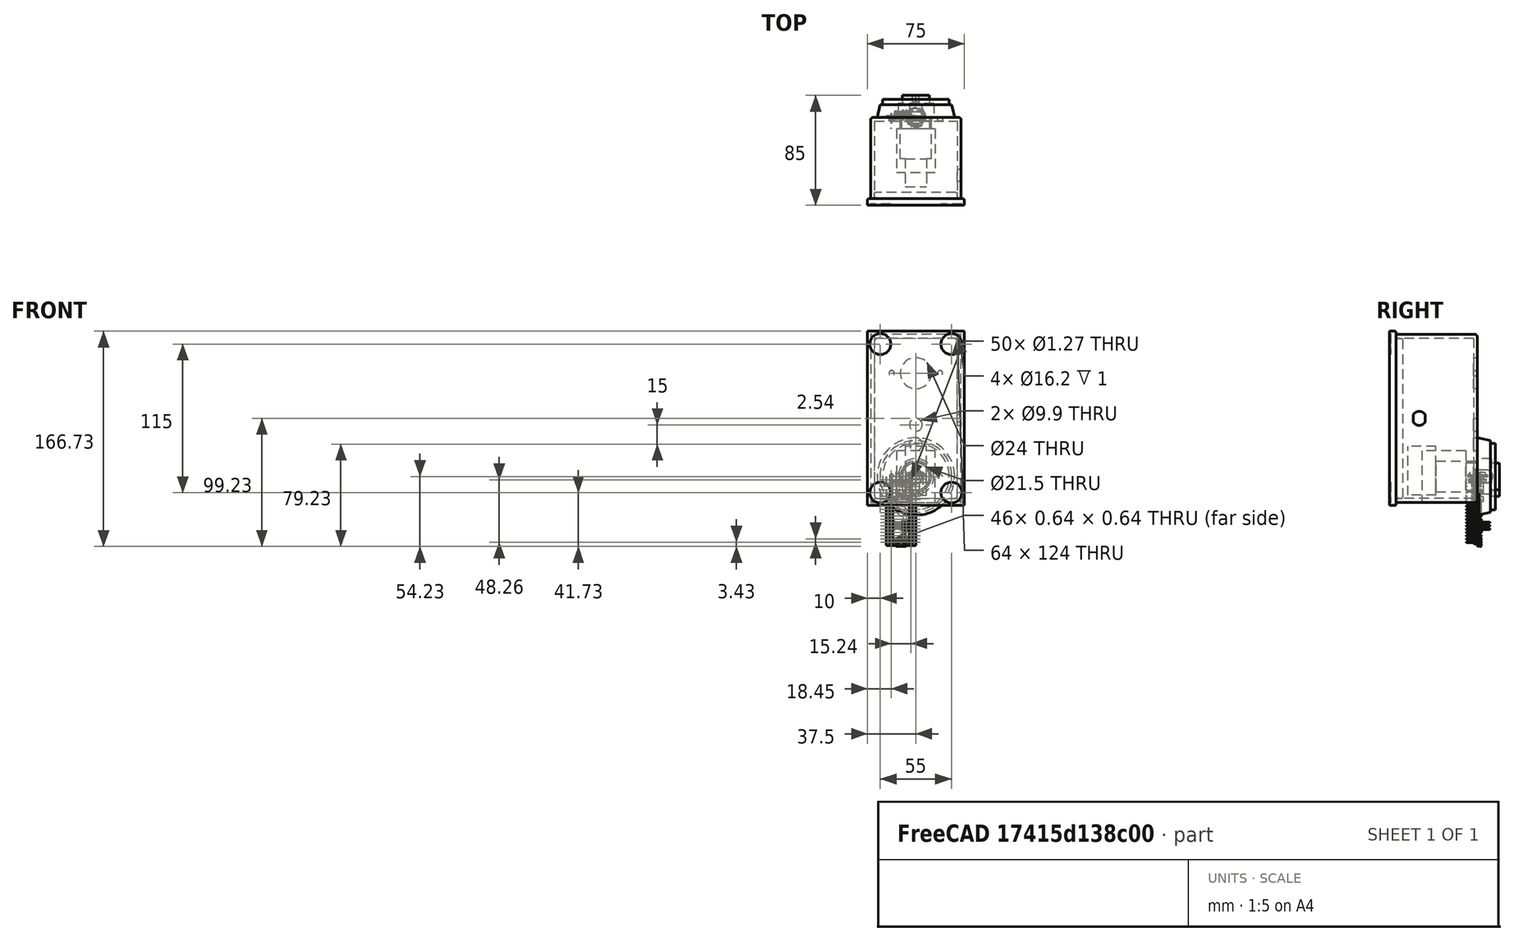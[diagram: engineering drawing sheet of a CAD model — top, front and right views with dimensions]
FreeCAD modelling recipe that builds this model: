
FCSTD DOCUMENT  (FreeCAD 1.0R39285 (Git))
Label: PDU
License: All rights reserved
LicenseURL: https://en.wikipedia.org/wiki/All_rights_reserved
objects: Part::Feature×108, Sketcher::SketchObject×21, PartDesign::Pad×13, App::Part×11, PartDesign::Body×11, PartDesign::SubShapeBinder×8, PartDesign::Revolution×5, PartDesign::Pocket×3, PartDesign::Fillet×2, Assembly::JointGroup×1, Assembly::AssemblyObject×1, PartDesign::ShapeBinder×1
note: 239 computed .brp shape members not serialized (recipe doc carries the construction recipe); baked Part::Feature solids carry a one-line shape summary decoded from their .brp

FEATURE [Part::Feature] Part__Feature  label="Oscillator_HC-49/S v1"
  Placement = pos=(-11.43,1.27,-17.526) rot=(0,1,0;1.5708rad)
  shape: bbox 11.35 x 5.5 x 5 mm, 15 faces (baked)
FEATURE [Part::Feature] Part__Feature001  label="STM32F103C8T6_BluePill_Board v6"
  shape: bbox 22.86 x 1.27 x 53.34 mm, 60 faces (baked)
FEATURE [Part::Feature] Part__Feature002  label="Oscillator_MC-306 v3"
  Placement = pos=(-11.43,1.43,-12.192) rot=(0,-1,0;1.5708rad)
  shape: bbox 8 x 2.38 x 3.2 mm, 30 faces (baked)
FEATURE [Part::Feature] Part__Feature003  label="Oscillator_MC-306 v004"
  Placement = pos=(-11.43,1.43,-12.192) rot=(0,-1,0;1.5708rad)
  shape: bbox 0.5 x 1.01 x 3.8 mm, 18 faces (baked)
FEATURE [Part::Feature] Part__Feature004  label="Oscillator_MC-306 v005"
  Placement = pos=(-11.43,1.43,-12.192) rot=(0,-1,0;1.5708rad)
  shape: bbox 0.5 x 1.01 x 3.8 mm, 18 faces (baked)
FEATURE [App::Part] Oscillator_MC_306_v3  label="Oscillator_MC-306 v006"
  Group = -> [Part__Feature002,Part__Feature003,Part__Feature004]
  Origin = -> Origin
FEATURE [Part::Feature] Part__Feature005  label="STM32_LQFP48 v3"
  Placement = pos=(-11.43,1.27,-26.162) rot=(0,1,0;0.785398rad)
  shape: bbox 9.899 x 1.6 x 9.899 mm, 6 faces (baked)
FEATURE [Part::Feature] Part__Feature006  label="Tactile_SMD_5x5mm v1"
  Placement = pos=(-14.43,1.3192,-38) rot=(0.57735,0.57735,0.57735;4.18879rad)
  shape: bbox 5.081 x 1.525 x 6.501 mm, 70 faces (baked)
FEATURE [Part::Feature] Part__Feature007  label="micro_usb_socket v1"
  Placement = pos=(-11.43,1.535,-53.8) rot=(0,1,0;3.14159rad)
  shape: bbox 10.2 x 2.83 x 7.23 mm, 434 faces (baked)
FEATURE [Part::Feature] Part__Feature008  label="Header_L4_10x4.8 v6"
  Placement = pos=(-11.43,2.54,-2.67) rot=(0,0.707107,-0.707107;3.14159rad)
  shape: bbox 2.54 x 2.54 x 2.5 mm, 26 faces (baked)
FEATURE [Part::Feature] Part__Feature009  label="Header_L4_10x4.8 v007"
  Placement = pos=(-11.43,2.54,-2.67) rot=(0,0.707107,-0.707107;3.14159rad)
  shape: bbox 0.64 x 4.8 x 10 mm, 18 faces (baked)
FEATURE [Part::Feature] Part__Feature010  label="Header_L4_10x4.8 v008"
  Placement = pos=(-11.43,2.54,-2.67) rot=(0,0.707107,-0.707107;3.14159rad)
  shape: bbox 2.54 x 2.54 x 2.5 mm, 26 faces (baked)
FEATURE [Part::Feature] Part__Feature011  label="Header_L4_10x4.8 v009"
  Placement = pos=(-11.43,2.54,-2.67) rot=(0,0.707107,-0.707107;3.14159rad)
  shape: bbox 2.54 x 2.54 x 2.5 mm, 26 faces (baked)
FEATURE [Part::Feature] Part__Feature012  label="Header_L4_10x4.8 v010"
  Placement = pos=(-11.43,2.54,-2.67) rot=(0,0.707107,-0.707107;3.14159rad)
  shape: bbox 2.54 x 2.54 x 2.5 mm, 26 faces (baked)
FEATURE [Part::Feature] Part__Feature013  label="Header_L4_10x4.8 v011"
  Placement = pos=(-11.43,2.54,-2.67) rot=(0,0.707107,-0.707107;3.14159rad)
  shape: bbox 0.64 x 4.8 x 10 mm, 18 faces (baked)
FEATURE [Part::Feature] Part__Feature014  label="Header_L4_10x4.8 v012"
  Placement = pos=(-11.43,2.54,-2.67) rot=(0,0.707107,-0.707107;3.14159rad)
  shape: bbox 0.64 x 4.8 x 10 mm, 18 faces (baked)
FEATURE [Part::Feature] Part__Feature015  label="Header_L4_10x4.8 v013"
  Placement = pos=(-11.43,2.54,-2.67) rot=(0,0.707107,-0.707107;3.14159rad)
  shape: bbox 0.64 x 4.8 x 10 mm, 18 faces (baked)
FEATURE [App::Part] Header_L4_10x4_8_v6  label="Header_L4_10x4.8 v014"
  Group = -> [Part__Feature008,Part__Feature009,Part__Feature010,Part__Feature011,Part__Feature012,Part__Feature013,Part__Feature014,Part__Feature015]
  Origin = -> Origin001
FEATURE [Part::Feature] Part__Feature016  label="Header_Male_2x3x11.6 v2"
  Placement = pos=(-8.636,1.27,-38.354) rot=(0,1,0;1.5708rad)
  shape: bbox 2.54 x 2.5 x 2.54 mm, 26 faces (baked)
FEATURE [Part::Feature] Part__Feature017  label="Header_Male_2x3x11.6 v003"
  Placement = pos=(-8.636,1.27,-38.354) rot=(0,1,0;1.5708rad)
  shape: bbox 0.64 x 11.6 x 0.64 mm, 14 faces (baked)
FEATURE [Part::Feature] Part__Feature018  label="Header_Male_2x3x11.6 v004"
  Placement = pos=(-8.636,1.27,-38.354) rot=(0,1,0;1.5708rad)
  shape: bbox 2.54 x 2.5 x 2.54 mm, 26 faces (baked)
FEATURE [Part::Feature] Part__Feature019  label="Header_Male_2x3x11.6 v005"
  Placement = pos=(-8.636,1.27,-38.354) rot=(0,1,0;1.5708rad)
  shape: bbox 2.54 x 2.5 x 2.54 mm, 26 faces (baked)
FEATURE [Part::Feature] Part__Feature020  label="Header_Male_2x3x11.6 v006"
  Placement = pos=(-8.636,1.27,-38.354) rot=(0,1,0;1.5708rad)
  shape: bbox 2.54 x 2.5 x 2.54 mm, 26 faces (baked)
FEATURE [Part::Feature] Part__Feature021  label="Header_Male_2x3x11.6 v007"
  Placement = pos=(-8.636,1.27,-38.354) rot=(0,1,0;1.5708rad)
  shape: bbox 2.54 x 2.5 x 2.54 mm, 26 faces (baked)
FEATURE [Part::Feature] Part__Feature022  label="Header_Male_2x3x11.6 v008"
  Placement = pos=(-8.636,1.27,-38.354) rot=(0,1,0;1.5708rad)
  shape: bbox 2.54 x 2.5 x 2.54 mm, 26 faces (baked)
FEATURE [Part::Feature] Part__Feature023  label="Header_Male_2x3x11.6 v009"
  Placement = pos=(-8.636,1.27,-38.354) rot=(0,1,0;1.5708rad)
  shape: bbox 0.64 x 11.6 x 0.64 mm, 14 faces (baked)
FEATURE [Part::Feature] Part__Feature024  label="Header_Male_2x3x11.6 v010"
  Placement = pos=(-8.636,1.27,-38.354) rot=(0,1,0;1.5708rad)
  shape: bbox 0.64 x 11.6 x 0.64 mm, 14 faces (baked)
FEATURE [Part::Feature] Part__Feature025  label="Header_Male_2x3x11.6 v011"
  Placement = pos=(-8.636,1.27,-38.354) rot=(0,1,0;1.5708rad)
  shape: bbox 0.64 x 11.6 x 0.64 mm, 14 faces (baked)
FEATURE [Part::Feature] Part__Feature026  label="Header_Male_2x3x11.6 v012"
  Placement = pos=(-8.636,1.27,-38.354) rot=(0,1,0;1.5708rad)
  shape: bbox 0.64 x 11.6 x 0.64 mm, 14 faces (baked)
FEATURE [Part::Feature] Part__Feature027  label="Header_Male_2x3x11.6 v013"
  Placement = pos=(-8.636,1.27,-38.354) rot=(0,1,0;1.5708rad)
  shape: bbox 0.64 x 11.6 x 0.64 mm, 14 faces (baked)
FEATURE [App::Part] Header_Male_2x3x11_6_v2  label="Header_Male_2x3x11.6 v014"
  Group = -> [Part__Feature016,Part__Feature017,Part__Feature018,Part__Feature019,Part__Feature020,Part__Feature021,Part__Feature022,Part__Feature023,Part__Feature024,Part__Feature025,Part__Feature026,Part__Feature027]
  Origin = -> Origin002
FEATURE [Part::Feature] Part__Feature028  label="Header_Male_1x20x11.6 v2"
  Placement = pos=(-3.81,2.2e-15,-26.67) rot=(0.707107,0,0.707107;3.14159rad)
  shape: bbox 2.54 x 2.5 x 2.54 mm, 26 faces (baked)
FEATURE [Part::Feature] Part__Feature029  label="Header_Male_1x20x11.6 v003"
  Placement = pos=(-3.81,2.2e-15,-26.67) rot=(0.707107,0,0.707107;3.14159rad)
  shape: bbox 0.64 x 11.6 x 0.64 mm, 14 faces (baked)
FEATURE [Part::Feature] Part__Feature030  label="Header_Male_1x20x11.6 v004"
  Placement = pos=(-3.81,2.2e-15,-26.67) rot=(0.707107,0,0.707107;3.14159rad)
  shape: bbox 2.54 x 2.5 x 2.54 mm, 26 faces (baked)
FEATURE [Part::Feature] Part__Feature031  label="Header_Male_1x20x11.6 v005"
  Placement = pos=(-3.81,2.2e-15,-26.67) rot=(0.707107,0,0.707107;3.14159rad)
  shape: bbox 2.54 x 2.5 x 2.54 mm, 26 faces (baked)
FEATURE [Part::Feature] Part__Feature032  label="Header_Male_1x20x11.6 v006"
  Placement = pos=(-3.81,2.2e-15,-26.67) rot=(0.707107,0,0.707107;3.14159rad)
  shape: bbox 2.54 x 2.5 x 2.54 mm, 26 faces (baked)
FEATURE [Part::Feature] Part__Feature033  label="Header_Male_1x20x11.6 v007"
  Placement = pos=(-3.81,2.2e-15,-26.67) rot=(0.707107,0,0.707107;3.14159rad)
  shape: bbox 2.54 x 2.5 x 2.54 mm, 26 faces (baked)
FEATURE [Part::Feature] Part__Feature034  label="Header_Male_1x20x11.6 v008"
  Placement = pos=(-3.81,2.2e-15,-26.67) rot=(0.707107,0,0.707107;3.14159rad)
  shape: bbox 2.54 x 2.5 x 2.54 mm, 26 faces (baked)
FEATURE [Part::Feature] Part__Feature035  label="Header_Male_1x20x11.6 v009"
  Placement = pos=(-3.81,2.2e-15,-26.67) rot=(0.707107,0,0.707107;3.14159rad)
  shape: bbox 2.54 x 2.5 x 2.54 mm, 26 faces (baked)
FEATURE [Part::Feature] Part__Feature036  label="Header_Male_1x20x11.6 v010"
  Placement = pos=(-3.81,2.2e-15,-26.67) rot=(0.707107,0,0.707107;3.14159rad)
  shape: bbox 2.54 x 2.5 x 2.54 mm, 26 faces (baked)
FEATURE [Part::Feature] Part__Feature037  label="Header_Male_1x20x11.6 v011"
  Placement = pos=(-3.81,2.2e-15,-26.67) rot=(0.707107,0,0.707107;3.14159rad)
  shape: bbox 2.54 x 2.5 x 2.54 mm, 26 faces (baked)
FEATURE [Part::Feature] Part__Feature038  label="Header_Male_1x20x11.6 v012"
  Placement = pos=(-3.81,2.2e-15,-26.67) rot=(0.707107,0,0.707107;3.14159rad)
  shape: bbox 2.54 x 2.5 x 2.54 mm, 26 faces (baked)
FEATURE [Part::Feature] Part__Feature039  label="Header_Male_1x20x11.6 v013"
  Placement = pos=(-3.81,2.2e-15,-26.67) rot=(0.707107,0,0.707107;3.14159rad)
  shape: bbox 2.54 x 2.5 x 2.54 mm, 26 faces (baked)
FEATURE [Part::Feature] Part__Feature040  label="Header_Male_1x20x11.6 v014"
  Placement = pos=(-3.81,2.2e-15,-26.67) rot=(0.707107,0,0.707107;3.14159rad)
  shape: bbox 2.54 x 2.5 x 2.54 mm, 26 faces (baked)
FEATURE [Part::Feature] Part__Feature041  label="Header_Male_1x20x11.6 v015"
  Placement = pos=(-3.81,2.2e-15,-26.67) rot=(0.707107,0,0.707107;3.14159rad)
  shape: bbox 2.54 x 2.5 x 2.54 mm, 26 faces (baked)
FEATURE [Part::Feature] Part__Feature042  label="Header_Male_1x20x11.6 v016"
  Placement = pos=(-3.81,2.2e-15,-26.67) rot=(0.707107,0,0.707107;3.14159rad)
  shape: bbox 2.54 x 2.5 x 2.54 mm, 26 faces (baked)
FEATURE [Part::Feature] Part__Feature043  label="Header_Male_1x20x11.6 v017"
  Placement = pos=(-3.81,2.2e-15,-26.67) rot=(0.707107,0,0.707107;3.14159rad)
  shape: bbox 2.54 x 2.5 x 2.54 mm, 26 faces (baked)
FEATURE [Part::Feature] Part__Feature044  label="Header_Male_1x20x11.6 v018"
  Placement = pos=(-3.81,2.2e-15,-26.67) rot=(0.707107,0,0.707107;3.14159rad)
  shape: bbox 2.54 x 2.5 x 2.54 mm, 26 faces (baked)
FEATURE [Part::Feature] Part__Feature045  label="Header_Male_1x20x11.6 v019"
  Placement = pos=(-3.81,2.2e-15,-26.67) rot=(0.707107,0,0.707107;3.14159rad)
  shape: bbox 2.54 x 2.5 x 2.54 mm, 26 faces (baked)
FEATURE [Part::Feature] Part__Feature046  label="Header_Male_1x20x11.6 v020"
  Placement = pos=(-3.81,2.2e-15,-26.67) rot=(0.707107,0,0.707107;3.14159rad)
  shape: bbox 2.54 x 2.5 x 2.54 mm, 26 faces (baked)
FEATURE [Part::Feature] Part__Feature047  label="Header_Male_1x20x11.6 v021"
  Placement = pos=(-3.81,2.2e-15,-26.67) rot=(0.707107,0,0.707107;3.14159rad)
  shape: bbox 2.54 x 2.5 x 2.54 mm, 26 faces (baked)
FEATURE [Part::Feature] Part__Feature048  label="Header_Male_1x20x11.6 v022"
  Placement = pos=(-3.81,2.2e-15,-26.67) rot=(0.707107,0,0.707107;3.14159rad)
  shape: bbox 2.54 x 2.5 x 2.54 mm, 26 faces (baked)
FEATURE [Part::Feature] Part__Feature049  label="Header_Male_1x20x11.6 v023"
  Placement = pos=(-3.81,2.2e-15,-26.67) rot=(0.707107,0,0.707107;3.14159rad)
  shape: bbox 0.64 x 11.6 x 0.64 mm, 14 faces (baked)
FEATURE [Part::Feature] Part__Feature050  label="Header_Male_1x20x11.6 v024"
  Placement = pos=(-3.81,2.2e-15,-26.67) rot=(0.707107,0,0.707107;3.14159rad)
  shape: bbox 0.64 x 11.6 x 0.64 mm, 14 faces (baked)
FEATURE [Part::Feature] Part__Feature051  label="Header_Male_1x20x11.6 v025"
  Placement = pos=(-3.81,2.2e-15,-26.67) rot=(0.707107,0,0.707107;3.14159rad)
  shape: bbox 0.64 x 11.6 x 0.64 mm, 14 faces (baked)
FEATURE [Part::Feature] Part__Feature052  label="Header_Male_1x20x11.6 v026"
  Placement = pos=(-3.81,2.2e-15,-26.67) rot=(0.707107,0,0.707107;3.14159rad)
  shape: bbox 0.64 x 11.6 x 0.64 mm, 14 faces (baked)
FEATURE [Part::Feature] Part__Feature053  label="Header_Male_1x20x11.6 v027"
  Placement = pos=(-3.81,2.2e-15,-26.67) rot=(0.707107,0,0.707107;3.14159rad)
  shape: bbox 0.64 x 11.6 x 0.64 mm, 14 faces (baked)
FEATURE [Part::Feature] Part__Feature054  label="Header_Male_1x20x11.6 v028"
  Placement = pos=(-3.81,2.2e-15,-26.67) rot=(0.707107,0,0.707107;3.14159rad)
  shape: bbox 0.64 x 11.6 x 0.64 mm, 14 faces (baked)
FEATURE [Part::Feature] Part__Feature055  label="Header_Male_1x20x11.6 v029"
  Placement = pos=(-3.81,2.2e-15,-26.67) rot=(0.707107,0,0.707107;3.14159rad)
  shape: bbox 0.64 x 11.6 x 0.64 mm, 14 faces (baked)
FEATURE [Part::Feature] Part__Feature056  label="Header_Male_1x20x11.6 v030"
  Placement = pos=(-3.81,2.2e-15,-26.67) rot=(0.707107,0,0.707107;3.14159rad)
  shape: bbox 0.64 x 11.6 x 0.64 mm, 14 faces (baked)
FEATURE [Part::Feature] Part__Feature057  label="Header_Male_1x20x11.6 v031"
  Placement = pos=(-3.81,2.2e-15,-26.67) rot=(0.707107,0,0.707107;3.14159rad)
  shape: bbox 0.64 x 11.6 x 0.64 mm, 14 faces (baked)
FEATURE [Part::Feature] Part__Feature058  label="Header_Male_1x20x11.6 v032"
  Placement = pos=(-3.81,2.2e-15,-26.67) rot=(0.707107,0,0.707107;3.14159rad)
  shape: bbox 0.64 x 11.6 x 0.64 mm, 14 faces (baked)
FEATURE [Part::Feature] Part__Feature059  label="Header_Male_1x20x11.6 v033"
  Placement = pos=(-3.81,2.2e-15,-26.67) rot=(0.707107,0,0.707107;3.14159rad)
  shape: bbox 0.64 x 11.6 x 0.64 mm, 14 faces (baked)
FEATURE [Part::Feature] Part__Feature060  label="Header_Male_1x20x11.6 v034"
  Placement = pos=(-3.81,2.2e-15,-26.67) rot=(0.707107,0,0.707107;3.14159rad)
  shape: bbox 0.64 x 11.6 x 0.64 mm, 14 faces (baked)
FEATURE [Part::Feature] Part__Feature061  label="Header_Male_1x20x11.6 v035"
  Placement = pos=(-3.81,2.2e-15,-26.67) rot=(0.707107,0,0.707107;3.14159rad)
  shape: bbox 0.64 x 11.6 x 0.64 mm, 14 faces (baked)
FEATURE [Part::Feature] Part__Feature062  label="Header_Male_1x20x11.6 v036"
  Placement = pos=(-3.81,2.2e-15,-26.67) rot=(0.707107,0,0.707107;3.14159rad)
  shape: bbox 0.64 x 11.6 x 0.64 mm, 14 faces (baked)
FEATURE [Part::Feature] Part__Feature063  label="Header_Male_1x20x11.6 v037"
  Placement = pos=(-3.81,2.2e-15,-26.67) rot=(0.707107,0,0.707107;3.14159rad)
  shape: bbox 0.64 x 11.6 x 0.64 mm, 14 faces (baked)
FEATURE [Part::Feature] Part__Feature064  label="Header_Male_1x20x11.6 v038"
  Placement = pos=(-3.81,2.2e-15,-26.67) rot=(0.707107,0,0.707107;3.14159rad)
  shape: bbox 0.64 x 11.6 x 0.64 mm, 14 faces (baked)
FEATURE [Part::Feature] Part__Feature065  label="Header_Male_1x20x11.6 v039"
  Placement = pos=(-3.81,2.2e-15,-26.67) rot=(0.707107,0,0.707107;3.14159rad)
  shape: bbox 0.64 x 11.6 x 0.64 mm, 14 faces (baked)
FEATURE [Part::Feature] Part__Feature066  label="Header_Male_1x20x11.6 v040"
  Placement = pos=(-3.81,2.2e-15,-26.67) rot=(0.707107,0,0.707107;3.14159rad)
  shape: bbox 0.64 x 11.6 x 0.64 mm, 14 faces (baked)
FEATURE [Part::Feature] Part__Feature067  label="Header_Male_1x20x11.6 v041"
  Placement = pos=(-3.81,2.2e-15,-26.67) rot=(0.707107,0,0.707107;3.14159rad)
  shape: bbox 0.64 x 11.6 x 0.64 mm, 14 faces (baked)
FEATURE [App::Part] Header_Male_1x20x11_6_v2  label="Header_Male_1x20x11.6 v042"
  Group = -> [Part__Feature028,Part__Feature029,Part__Feature030,Part__Feature031,Part__Feature032,Part__Feature033,Part__Feature034,Part__Feature035,Part__Feature036,Part__Feature037,Part__Feature038,Part__Feature039,Part__Feature040,Part__Feature041,Part__Feature042,Part__Feature043,Part__Feature044,Part__Feature045,Part__Feature046,Part__Feature047,Part__Feature048,Part__Feature049,Part__Feature050,+17 more]
  Origin = -> Origin003
FEATURE [Part::Feature] Part__Feature068  label="Header_Male_1x20x11.6 v043"
  Placement = pos=(-19.05,2.2e-15,-26.67) rot=(0.707107,0,0.707107;3.14159rad)
  shape: bbox 2.54 x 2.5 x 2.54 mm, 26 faces (baked)
FEATURE [Part::Feature] Part__Feature069  label="Header_Male_1x20x11.6 v044"
  Placement = pos=(-19.05,2.2e-15,-26.67) rot=(0.707107,0,0.707107;3.14159rad)
  shape: bbox 0.64 x 11.6 x 0.64 mm, 14 faces (baked)
FEATURE [Part::Feature] Part__Feature070  label="Header_Male_1x20x11.6 v045"
  Placement = pos=(-19.05,2.2e-15,-26.67) rot=(0.707107,0,0.707107;3.14159rad)
  shape: bbox 2.54 x 2.5 x 2.54 mm, 26 faces (baked)
FEATURE [Part::Feature] Part__Feature071  label="Header_Male_1x20x11.6 v046"
  Placement = pos=(-19.05,2.2e-15,-26.67) rot=(0.707107,0,0.707107;3.14159rad)
  shape: bbox 2.54 x 2.5 x 2.54 mm, 26 faces (baked)
FEATURE [Part::Feature] Part__Feature072  label="Header_Male_1x20x11.6 v047"
  Placement = pos=(-19.05,2.2e-15,-26.67) rot=(0.707107,0,0.707107;3.14159rad)
  shape: bbox 2.54 x 2.5 x 2.54 mm, 26 faces (baked)
FEATURE [Part::Feature] Part__Feature073  label="Header_Male_1x20x11.6 v048"
  Placement = pos=(-19.05,2.2e-15,-26.67) rot=(0.707107,0,0.707107;3.14159rad)
  shape: bbox 2.54 x 2.5 x 2.54 mm, 26 faces (baked)
FEATURE [Part::Feature] Part__Feature074  label="Header_Male_1x20x11.6 v049"
  Placement = pos=(-19.05,2.2e-15,-26.67) rot=(0.707107,0,0.707107;3.14159rad)
  shape: bbox 2.54 x 2.5 x 2.54 mm, 26 faces (baked)
FEATURE [Part::Feature] Part__Feature075  label="Header_Male_1x20x11.6 v050"
  Placement = pos=(-19.05,2.2e-15,-26.67) rot=(0.707107,0,0.707107;3.14159rad)
  shape: bbox 2.54 x 2.5 x 2.54 mm, 26 faces (baked)
FEATURE [Part::Feature] Part__Feature076  label="Header_Male_1x20x11.6 v051"
  Placement = pos=(-19.05,2.2e-15,-26.67) rot=(0.707107,0,0.707107;3.14159rad)
  shape: bbox 2.54 x 2.5 x 2.54 mm, 26 faces (baked)
FEATURE [Part::Feature] Part__Feature077  label="Header_Male_1x20x11.6 v052"
  Placement = pos=(-19.05,2.2e-15,-26.67) rot=(0.707107,0,0.707107;3.14159rad)
  shape: bbox 2.54 x 2.5 x 2.54 mm, 26 faces (baked)
FEATURE [Part::Feature] Part__Feature078  label="Header_Male_1x20x11.6 v053"
  Placement = pos=(-19.05,2.2e-15,-26.67) rot=(0.707107,0,0.707107;3.14159rad)
  shape: bbox 2.54 x 2.5 x 2.54 mm, 26 faces (baked)
FEATURE [Part::Feature] Part__Feature079  label="Header_Male_1x20x11.6 v054"
  Placement = pos=(-19.05,2.2e-15,-26.67) rot=(0.707107,0,0.707107;3.14159rad)
  shape: bbox 2.54 x 2.5 x 2.54 mm, 26 faces (baked)
FEATURE [Part::Feature] Part__Feature080  label="Header_Male_1x20x11.6 v055"
  Placement = pos=(-19.05,2.2e-15,-26.67) rot=(0.707107,0,0.707107;3.14159rad)
  shape: bbox 2.54 x 2.5 x 2.54 mm, 26 faces (baked)
FEATURE [Part::Feature] Part__Feature081  label="Header_Male_1x20x11.6 v056"
  Placement = pos=(-19.05,2.2e-15,-26.67) rot=(0.707107,0,0.707107;3.14159rad)
  shape: bbox 2.54 x 2.5 x 2.54 mm, 26 faces (baked)
FEATURE [Part::Feature] Part__Feature082  label="Header_Male_1x20x11.6 v057"
  Placement = pos=(-19.05,2.2e-15,-26.67) rot=(0.707107,0,0.707107;3.14159rad)
  shape: bbox 2.54 x 2.5 x 2.54 mm, 26 faces (baked)
FEATURE [Part::Feature] Part__Feature083  label="Header_Male_1x20x11.6 v058"
  Placement = pos=(-19.05,2.2e-15,-26.67) rot=(0.707107,0,0.707107;3.14159rad)
  shape: bbox 2.54 x 2.5 x 2.54 mm, 26 faces (baked)
FEATURE [Part::Feature] Part__Feature084  label="Header_Male_1x20x11.6 v059"
  Placement = pos=(-19.05,2.2e-15,-26.67) rot=(0.707107,0,0.707107;3.14159rad)
  shape: bbox 2.54 x 2.5 x 2.54 mm, 26 faces (baked)
FEATURE [Part::Feature] Part__Feature085  label="Header_Male_1x20x11.6 v060"
  Placement = pos=(-19.05,2.2e-15,-26.67) rot=(0.707107,0,0.707107;3.14159rad)
  shape: bbox 2.54 x 2.5 x 2.54 mm, 26 faces (baked)
FEATURE [Part::Feature] Part__Feature086  label="Header_Male_1x20x11.6 v061"
  Placement = pos=(-19.05,2.2e-15,-26.67) rot=(0.707107,0,0.707107;3.14159rad)
  shape: bbox 2.54 x 2.5 x 2.54 mm, 26 faces (baked)
FEATURE [Part::Feature] Part__Feature087  label="Header_Male_1x20x11.6 v062"
  Placement = pos=(-19.05,2.2e-15,-26.67) rot=(0.707107,0,0.707107;3.14159rad)
  shape: bbox 2.54 x 2.5 x 2.54 mm, 26 faces (baked)
FEATURE [Part::Feature] Part__Feature088  label="Header_Male_1x20x11.6 v063"
  Placement = pos=(-19.05,2.2e-15,-26.67) rot=(0.707107,0,0.707107;3.14159rad)
  shape: bbox 2.54 x 2.5 x 2.54 mm, 26 faces (baked)
FEATURE [Part::Feature] Part__Feature089  label="Header_Male_1x20x11.6 v064"
  Placement = pos=(-19.05,2.2e-15,-26.67) rot=(0.707107,0,0.707107;3.14159rad)
  shape: bbox 0.64 x 11.6 x 0.64 mm, 14 faces (baked)
FEATURE [Part::Feature] Part__Feature090  label="Header_Male_1x20x11.6 v065"
  Placement = pos=(-19.05,2.2e-15,-26.67) rot=(0.707107,0,0.707107;3.14159rad)
  shape: bbox 0.64 x 11.6 x 0.64 mm, 14 faces (baked)
FEATURE [Part::Feature] Part__Feature091  label="Header_Male_1x20x11.6 v066"
  Placement = pos=(-19.05,2.2e-15,-26.67) rot=(0.707107,0,0.707107;3.14159rad)
  shape: bbox 0.64 x 11.6 x 0.64 mm, 14 faces (baked)
FEATURE [Part::Feature] Part__Feature092  label="Header_Male_1x20x11.6 v067"
  Placement = pos=(-19.05,2.2e-15,-26.67) rot=(0.707107,0,0.707107;3.14159rad)
  shape: bbox 0.64 x 11.6 x 0.64 mm, 14 faces (baked)
FEATURE [Part::Feature] Part__Feature093  label="Header_Male_1x20x11.6 v068"
  Placement = pos=(-19.05,2.2e-15,-26.67) rot=(0.707107,0,0.707107;3.14159rad)
  shape: bbox 0.64 x 11.6 x 0.64 mm, 14 faces (baked)
FEATURE [Part::Feature] Part__Feature094  label="Header_Male_1x20x11.6 v069"
  Placement = pos=(-19.05,2.2e-15,-26.67) rot=(0.707107,0,0.707107;3.14159rad)
  shape: bbox 0.64 x 11.6 x 0.64 mm, 14 faces (baked)
FEATURE [Part::Feature] Part__Feature095  label="Header_Male_1x20x11.6 v070"
  Placement = pos=(-19.05,2.2e-15,-26.67) rot=(0.707107,0,0.707107;3.14159rad)
  shape: bbox 0.64 x 11.6 x 0.64 mm, 14 faces (baked)
FEATURE [Part::Feature] Part__Feature096  label="Header_Male_1x20x11.6 v071"
  Placement = pos=(-19.05,2.2e-15,-26.67) rot=(0.707107,0,0.707107;3.14159rad)
  shape: bbox 0.64 x 11.6 x 0.64 mm, 14 faces (baked)
FEATURE [Part::Feature] Part__Feature097  label="Header_Male_1x20x11.6 v072"
  Placement = pos=(-19.05,2.2e-15,-26.67) rot=(0.707107,0,0.707107;3.14159rad)
  shape: bbox 0.64 x 11.6 x 0.64 mm, 14 faces (baked)
FEATURE [Part::Feature] Part__Feature098  label="Header_Male_1x20x11.6 v073"
  Placement = pos=(-19.05,2.2e-15,-26.67) rot=(0.707107,0,0.707107;3.14159rad)
  shape: bbox 0.64 x 11.6 x 0.64 mm, 14 faces (baked)
FEATURE [Part::Feature] Part__Feature099  label="Header_Male_1x20x11.6 v074"
  Placement = pos=(-19.05,2.2e-15,-26.67) rot=(0.707107,0,0.707107;3.14159rad)
  shape: bbox 0.64 x 11.6 x 0.64 mm, 14 faces (baked)
FEATURE [Part::Feature] Part__Feature100  label="Header_Male_1x20x11.6 v075"
  Placement = pos=(-19.05,2.2e-15,-26.67) rot=(0.707107,0,0.707107;3.14159rad)
  shape: bbox 0.64 x 11.6 x 0.64 mm, 14 faces (baked)
FEATURE [Part::Feature] Part__Feature101  label="Header_Male_1x20x11.6 v076"
  Placement = pos=(-19.05,2.2e-15,-26.67) rot=(0.707107,0,0.707107;3.14159rad)
  shape: bbox 0.64 x 11.6 x 0.64 mm, 14 faces (baked)
FEATURE [Part::Feature] Part__Feature102  label="Header_Male_1x20x11.6 v077"
  Placement = pos=(-19.05,2.2e-15,-26.67) rot=(0.707107,0,0.707107;3.14159rad)
  shape: bbox 0.64 x 11.6 x 0.64 mm, 14 faces (baked)
FEATURE [Part::Feature] Part__Feature103  label="Header_Male_1x20x11.6 v078"
  Placement = pos=(-19.05,2.2e-15,-26.67) rot=(0.707107,0,0.707107;3.14159rad)
  shape: bbox 0.64 x 11.6 x 0.64 mm, 14 faces (baked)
FEATURE [Part::Feature] Part__Feature104  label="Header_Male_1x20x11.6 v079"
  Placement = pos=(-19.05,2.2e-15,-26.67) rot=(0.707107,0,0.707107;3.14159rad)
  shape: bbox 0.64 x 11.6 x 0.64 mm, 14 faces (baked)
FEATURE [Part::Feature] Part__Feature105  label="Header_Male_1x20x11.6 v080"
  Placement = pos=(-19.05,2.2e-15,-26.67) rot=(0.707107,0,0.707107;3.14159rad)
  shape: bbox 0.64 x 11.6 x 0.64 mm, 14 faces (baked)
FEATURE [Part::Feature] Part__Feature106  label="Header_Male_1x20x11.6 v081"
  Placement = pos=(-19.05,2.2e-15,-26.67) rot=(0.707107,0,0.707107;3.14159rad)
  shape: bbox 0.64 x 11.6 x 0.64 mm, 14 faces (baked)
FEATURE [Part::Feature] Part__Feature107  label="Header_Male_1x20x11.6 v082"
  Placement = pos=(-19.05,2.2e-15,-26.67) rot=(0.707107,0,0.707107;3.14159rad)
  shape: bbox 0.64 x 11.6 x 0.64 mm, 14 faces (baked)
FEATURE [App::Part] Header_Male_1x20x11_6_v003  label="Header_Male_1x20x11.6 v083"
  Group = -> [Part__Feature068,Part__Feature069,Part__Feature070,Part__Feature071,Part__Feature072,Part__Feature073,Part__Feature074,Part__Feature075,Part__Feature076,Part__Feature077,Part__Feature078,Part__Feature079,Part__Feature080,Part__Feature081,Part__Feature082,Part__Feature083,Part__Feature084,Part__Feature085,Part__Feature086,Part__Feature087,Part__Feature088,Part__Feature089,Part__Feature090,+17 more]
  Origin = -> Origin004
FEATURE [App::Part] STM32F103C8T6_Blue_Pill_v6  label="STM32F103C8T6_Blue_Pill v6"
  Group = -> [Part__Feature,Part__Feature001,Oscillator_MC_306_v3,Part__Feature005,Part__Feature006,Part__Feature007,Header_L4_10x4_8_v6,Header_Male_2x3x11_6_v2,Header_Male_1x20x11_6_v2,Header_Male_1x20x11_6_v003]
  Origin = -> Origin005
  Placement = pos=(-25,-61,76) rot=(0,0,-1;1.5708rad)
FEATURE [Assembly::JointGroup] Joints
FEATURE [Sketcher::SketchObject] Sketch011
  ArcFitTolerance = 1e-06
  AttachmentSupport = -> [XY_Plane010]
  FullyConstrained = true
  MakeInternals = false
  MapMode = 5
  sketch-geometry (2):
    g0: Circle CenterX=0 CenterY=0 CenterZ=0 NormalX=0 NormalY=0 NormalZ=1 AngleXU=0 Radius=7.75
    g1: Circle CenterX=0 CenterY=0 CenterZ=0 NormalX=0 NormalY=0 NormalZ=1 AngleXU=0 Radius=5.4
  constraints (4):
    c: Diameter(g0) = 15.5
    c: Coincident(g0,g-1)
    c: Diameter(g1) = 10.8
    c: Coincident(g1,g0)
FEATURE [PartDesign::Pad] Pad007
  Direction = (0,0,1)
  Length = 1
  Length2 = 10
  Profile = -> Sketch011
  ReferenceAxis = -> Sketch011 [N_Axis]
  Refine = true
  Suppressed = false
  Type = 0
FEATURE [PartDesign::Body] Body004  label="Rubber"
  AllowCompound = false
  Group = -> [Sketch011,Pad007]
  Origin = -> Origin010
  Tip = -> Pad007
FEATURE [Sketcher::SketchObject] Sketch012
  ArcFitTolerance = 1e-06
  FullyConstrained = false
  MakeInternals = false
  sketch-geometry (8):
    g0: ArcOfCircle CenterX=0 CenterY=0 CenterZ=0 NormalX=0 NormalY=0 NormalZ=1 AngleXU=0 Radius=5.4 StartAngle=2.12208 EndAngle=3.14159
    g1: LineSegment StartX=0 StartY=4.6 StartZ=0 EndX=2.82843 EndY=4.6 EndZ=0
    g2: LineSegment StartX=0 StartY=4.6 StartZ=0 EndX=-2.82843 EndY=4.6 EndZ=0
    g3: ArcOfCircle CenterX=0 CenterY=0 CenterZ=0 NormalX=0 NormalY=0 NormalZ=1 AngleXU=0 Radius=5.4 StartAngle=-9e-16 EndAngle=1.01951
    g4: ArcOfCircle CenterX=0 CenterY=0 CenterZ=0 NormalX=0 NormalY=0 NormalZ=1 AngleXU=0 Radius=5.4 StartAngle=3.14159 EndAngle=4.1611
    g5: LineSegment StartX=0 StartY=-4.6 StartZ=0 EndX=-2.82843 EndY=-4.6 EndZ=0
    g6: LineSegment StartX=0 StartY=-4.6 StartZ=0 EndX=2.82843 EndY=-4.6 EndZ=0
    g7: ArcOfCircle CenterX=0 CenterY=0 CenterZ=0 NormalX=0 NormalY=0 NormalZ=1 AngleXU=0 Radius=5.4 StartAngle=5.26367 EndAngle=6.28319
  constraints (14):
    c: Diameter(g0) = 10.8
    c: Coincident(g0,g-1)
    c: PointOnObject(g1,g-2)
    c: Horizontal(g1)
    c: Coincident(g1,g3)
    c: Coincident(g2,g0)
    c: Equal(g0,g3)
    c: Coincident(g0,g3)
    c: Diameter(g4) = 10.8
    c: Horizontal(g6)
    c: Coincident(g6,g7)
    c: Coincident(g5,g4)
    c: Equal(g4,g7)
    c: Coincident(g4,g7)
FEATURE [PartDesign::Pad] Pad008
  Direction = (0,0,1)
  Length = 1
  Length2 = 10
  Profile = -> Sketch012
  ReferenceAxis = -> Sketch012 [N_Axis]
  Refine = true
  Suppressed = false
  Type = 0
FEATURE [Sketcher::SketchObject] Sketch013
  ArcFitTolerance = 1e-06
  FullyConstrained = false
  MakeInternals = false
  sketch-geometry (8):
    g0: ArcOfCircle CenterX=0 CenterY=0 CenterZ=0 NormalX=0 NormalY=0 NormalZ=1 AngleXU=0 Radius=5.4 StartAngle=2.12208 EndAngle=3.14159
    g1: LineSegment StartX=0 StartY=4.6 StartZ=0 EndX=2.82843 EndY=4.6 EndZ=0
    g2: LineSegment StartX=0 StartY=4.6 StartZ=0 EndX=-2.82843 EndY=4.6 EndZ=0
    g3: ArcOfCircle CenterX=0 CenterY=0 CenterZ=0 NormalX=0 NormalY=0 NormalZ=1 AngleXU=0 Radius=5.4 StartAngle=-9e-16 EndAngle=1.01951
    g4: ArcOfCircle CenterX=0 CenterY=0 CenterZ=0 NormalX=0 NormalY=0 NormalZ=1 AngleXU=0 Radius=5.4 StartAngle=3.14159 EndAngle=4.1611
    g5: LineSegment StartX=0 StartY=-4.6 StartZ=0 EndX=-2.82843 EndY=-4.6 EndZ=0
    g6: LineSegment StartX=0 StartY=-4.6 StartZ=0 EndX=2.82843 EndY=-4.6 EndZ=0
    g7: ArcOfCircle CenterX=0 CenterY=0 CenterZ=0 NormalX=0 NormalY=0 NormalZ=1 AngleXU=0 Radius=5.4 StartAngle=5.26367 EndAngle=6.28319
  constraints (14):
    c: Diameter(g0) = 10.8
    c: Coincident(g0,g-1)
    c: PointOnObject(g1,g-2)
    c: Horizontal(g1)
    c: Coincident(g1,g3)
    c: Coincident(g2,g0)
    c: Equal(g0,g3)
    c: Coincident(g0,g3)
    c: Diameter(g4) = 10.8
    c: Horizontal(g6)
    c: Coincident(g6,g7)
    c: Coincident(g5,g4)
    c: Equal(g4,g7)
    c: Coincident(g4,g7)
FEATURE [PartDesign::Pad] Pad009
  BaseFeature = -> Pad008
  Direction = (0,0,1)
  Length = 13.1
  Length2 = 10
  Profile = -> Sketch013
  ReferenceAxis = -> Sketch013 [N_Axis]
  Refine = true
  Reversed = true
  Suppressed = false
  Type = 0
FEATURE [Sketcher::SketchObject] Sketch014
  ArcFitTolerance = 1e-06
  AttachmentSupport = -> [YZ_Plane012]
  FullyConstrained = true
  MakeInternals = false
  MapMode = 5
  Placement = pos=(0,0,0) rot=(0.57735,0.57735,0.57735;2.0944rad)
  sketch-geometry (5):
    g0: LineSegment [constr] StartX=0 StartY=0 StartZ=0 EndX=0 EndY=1 EndZ=0
    g1: LineSegment StartX=0 StartY=1 StartZ=0 EndX=0 EndY=3 EndZ=0
    g2: LineSegment StartX=0 StartY=3 StartZ=0 EndX=5.9 EndY=3 EndZ=0
    g3: LineSegment StartX=0 StartY=1 StartZ=0 EndX=6.9 EndY=1 EndZ=0
    g4: LineSegment StartX=6.9 StartY=1 StartZ=0 EndX=5.9 EndY=3 EndZ=0
  constraints (14):
    c: Distance(g0) = 1
    c: Coincident(g0,g-1)
    c: PointOnObject(g0,g-2)
    c: Distance(g1) = 2
    c: Coincident(g1,g0)
    c: PointOnObject(g1,g-2)
    c: Distance(g2) = 5.9
    c: Coincident(g2,g1)
    c: Horizontal(g2)
    c: Distance(g3) = 6.9
    c: Coincident(g3,g0)
    c: Horizontal(g3)
    c: Coincident(g4,g3)
    c: Coincident(g4,g2)
FEATURE [PartDesign::Revolution] Revolution002
  Angle = 360
  Angle2 = 60
  Axis = (0,0,1)
  Base = (0,0,0)
  BaseFeature = -> Pad009
  Profile = -> Sketch014
  ReferenceAxis = -> Sketch014 [V_Axis]
  Refine = true
  Reversed = true
  Suppressed = false
  Type = 0
FEATURE [Sketcher::SketchObject] Sketch015
  ArcFitTolerance = 1e-06
  AttachmentSupport = -> [Revolution002]
  FullyConstrained = false
  MakeInternals = false
  MapMode = 5
  Placement = pos=(0,0,3) rot=(0,0,1;0rad)
  sketch-geometry (4):
    g0: ArcOfCircle CenterX=-3.315 CenterY=-8.55e-14 CenterZ=0 NormalX=0 NormalY=0 NormalZ=1 AngleXU=0 Radius=1.28 StartAngle=1.5708 EndAngle=4.71239
    g1: ArcOfCircle CenterX=3.315 CenterY=-8.55e-14 CenterZ=0 NormalX=0 NormalY=0 NormalZ=1 AngleXU=0 Radius=1.28 StartAngle=4.71239 EndAngle=7.85398
    g2: LineSegment StartX=-3.315 StartY=1.28 StartZ=0 EndX=3.315 EndY=1.28 EndZ=0
    g3: LineSegment StartX=-3.315 StartY=-1.28 StartZ=0 EndX=3.315 EndY=-1.28 EndZ=0
  constraints (9):
    c: PointOnObject(g0,g-1)
    c: Tangent(g0,g2) = 1.5708
    c: Tangent(g0,g3) = -1.5708
    c: Tangent(g1,g2) = 1.5708
    c: Tangent(g1,g3) = -1.5708
    c: Equal(g0,g1)
    c: Horizontal(g3)
    c: Distance(g0,g1) = 6.63
    c: Radius(g0) = 1.28
FEATURE [PartDesign::Pocket] Pocket001
  BaseFeature = -> Revolution002
  Direction = (0,0,-1)
  Length = 1
  Length2 = 5
  Profile = -> Sketch015
  ReferenceAxis = -> Sketch015 [N_Axis]
  Refine = true
  Suppressed = false
  Type = 0
FEATURE [PartDesign::Body] Body005  label="House"
  AllowCompound = false
  Group = -> [Sketch012,Sketch013,Pad008,Pad009,Sketch014,Revolution002,Sketch015,Pocket001]
  Origin = -> Origin012
  Tip = -> Pocket001
FEATURE [Sketcher::SketchObject] Sketch016
  ArcFitTolerance = 1e-06
  AttachmentSupport = -> [XY_Plane013]
  FullyConstrained = true
  MakeInternals = false
  MapMode = 5
  sketch-geometry (8):
    g0: LineSegment StartX=7.75 StartY=0 StartZ=0 EndX=3.875 EndY=6.7117 EndZ=0
    g1: LineSegment StartX=3.875 StartY=6.7117 StartZ=0 EndX=-3.875 EndY=6.7117 EndZ=0
    g2: LineSegment StartX=-3.875 StartY=6.7117 StartZ=0 EndX=-7.75 EndY=9e-16 EndZ=0
    g3: LineSegment StartX=-7.75 StartY=9e-16 StartZ=0 EndX=-3.875 EndY=-6.7117 EndZ=0
    g4: LineSegment StartX=-3.875 StartY=-6.7117 StartZ=0 EndX=3.875 EndY=-6.7117 EndZ=0
    g5: LineSegment StartX=3.875 StartY=-6.7117 StartZ=0 EndX=7.75 EndY=0 EndZ=0
    g6: Circle [constr] CenterX=0 CenterY=0 CenterZ=0 NormalX=0 NormalY=0 NormalZ=1 AngleXU=0 Radius=7.75
    g7: Circle CenterX=0 CenterY=0 CenterZ=0 NormalX=0 NormalY=0 NormalZ=1 AngleXU=0 Radius=5.4
  constraints (18):
    c: Coincident(g0,g1)
    c: Coincident(g1,g2)
    c: Coincident(g2,g3)
    c: Coincident(g3,g4)
    c: Coincident(g4,g5)
    c: Coincident(g5,g0)
    c: Equal(g0, g1-g5) x5
    c: PointOnObject(g0,g6)
    c: PointOnObject(g1,g6)
    c: PointOnObject(g2,g6)
    c: PointOnObject(g3,g6)
    c: PointOnObject(g4,g6)
    c: PointOnObject(g5,g6)
    c: Radius(g6) = 7.75
    c: Coincident(g6,g-1)
    c: PointOnObject(g5,g-1)
    c: Diameter(g7) = 10.8
    c: Coincident(g7,g6)
FEATURE [PartDesign::Pad] Pad010
  Direction = (0,0,1)
  Length = 3
  Length2 = 10
  Profile = -> Sketch016
  ReferenceAxis = -> Sketch016 [N_Axis]
  Refine = true
  Reversed = true
  Suppressed = false
  Type = 0
FEATURE [PartDesign::Body] Body006  label="Skrew"
  AllowCompound = false
  Group = -> [Sketch016,Pad010]
  Origin = -> Origin013
  Placement = pos=(0,0,-2) rot=(0,0,1;0rad)
  Tip = -> Pad010
FEATURE [Assembly::AssemblyObject] Assembly  label="TypeCHousing"
  Group = -> [Joints,Body004,Body005,Body006]
  Origin = -> Origin011
  Placement = pos=(35,-45,45) rot=(0,1,0;1.5708rad)
  Type = Assembly
FEATURE [Sketcher::SketchObject] Sketch017
  ArcFitTolerance = 1e-06
  AttachmentSupport = -> [XY_Plane015]
  FullyConstrained = true
  MakeInternals = false
  MapMode = 5
  sketch-geometry (8):
    g0: LineSegment StartX=0 StartY=0 StartZ=0 EndX=3e-16 EndY=12 EndZ=0
    g1: LineSegment [constr] StartX=3e-16 StartY=12 StartZ=0 EndX=0 EndY=7.05 EndZ=0
    g2: ArcOfCircle CenterX=0 CenterY=7.05 CenterZ=0 NormalX=0 NormalY=0 NormalZ=1 AngleXU=0 Radius=4.95 StartAngle=3.26795e-07 EndAngle=1.5708
    g3: LineSegment StartX=4.95 StartY=7.05 StartZ=0 EndX=4.95 EndY=0 EndZ=0
    g4: LineSegment StartX=4.95 StartY=0 StartZ=0 EndX=5.5 EndY=0 EndZ=0
    g5: LineSegment StartX=5.5 StartY=0 StartZ=0 EndX=5.5 EndY=-2 EndZ=0
    g6: LineSegment StartX=5.5 StartY=-2 StartZ=0 EndX=0 EndY=-2 EndZ=0
    g7: LineSegment StartX=0 StartY=-2 StartZ=0 EndX=0 EndY=0 EndZ=0
  constraints (23):
    c: Distance(g0) = 12
    c: Coincident(g0,g-1)
    c: PointOnObject(g0,g-2)
    c: Distance(g1) = 4.95
    c: Coincident(g1,g0)
    c: PointOnObject(g1,g0)
    c: Angle(g2) = 1.5708
    c: Coincident(g2,g1)
    c: Coincident(g2,g0)
    c: Coincident(g3,g2)
    c: PointOnObject(g3,g-1)
    c: Vertical(g3)
    c: Distance(g4) = 0.55
    c: Coincident(g4,g3)
    c: PointOnObject(g4,g-1)
    c: Distance(g5) = 2
    c: Coincident(g5,g4)
    c: Vertical(g5)
    c: Coincident(g6,g5)
    c: PointOnObject(g6,g-2)
    c: Horizontal(g6)
    c: Coincident(g7,g6)
    c: Coincident(g7,g0)
FEATURE [PartDesign::Revolution] Revolution003
  Angle = 360
  Angle2 = 60
  Axis = (0,1,0)
  Base = (0,0,0)
  Profile = -> Sketch017
  ReferenceAxis = -> Sketch017 [V_Axis]
  Refine = true
  Reversed = true
  Suppressed = false
  Type = 0
FEATURE [PartDesign::Body] Body007  label="Body"
  AllowCompound = false
  Group = -> [Sketch017,Revolution003]
  Origin = -> Origin015
  Tip = -> Revolution003
FEATURE [App::Part] Part  label="Led10mm"
  Group = -> [Body007]
  Origin = -> Origin014
  Placement = pos=(0,-3,25) rot=(0,0,1;0rad)
FEATURE [Sketcher::SketchObject] Sketch018
  ArcFitTolerance = 1e-06
  AttachmentSupport = -> [XY_Plane017]
  FullyConstrained = true
  MakeInternals = false
  MapMode = 5
  sketch-geometry (8):
    g0: LineSegment StartX=0 StartY=0 StartZ=0 EndX=3e-16 EndY=12 EndZ=0
    g1: LineSegment [constr] StartX=3e-16 StartY=12 StartZ=0 EndX=0 EndY=7.05 EndZ=0
    g2: ArcOfCircle CenterX=0 CenterY=7.05 CenterZ=0 NormalX=0 NormalY=0 NormalZ=1 AngleXU=0 Radius=4.95 StartAngle=3.26795e-07 EndAngle=1.5708
    g3: LineSegment StartX=4.95 StartY=7.05 StartZ=0 EndX=4.95 EndY=0 EndZ=0
    g4: LineSegment StartX=4.95 StartY=0 StartZ=0 EndX=5.5 EndY=0 EndZ=0
    g5: LineSegment StartX=5.5 StartY=0 StartZ=0 EndX=5.5 EndY=-2 EndZ=0
    g6: LineSegment StartX=5.5 StartY=-2 StartZ=0 EndX=0 EndY=-2 EndZ=0
    g7: LineSegment StartX=0 StartY=-2 StartZ=0 EndX=0 EndY=0 EndZ=0
  constraints (23):
    c: Distance(g0) = 12
    c: Coincident(g0,g-1)
    c: PointOnObject(g0,g-2)
    c: Distance(g1) = 4.95
    c: Coincident(g1,g0)
    c: PointOnObject(g1,g0)
    c: Angle(g2) = 1.5708
    c: Coincident(g2,g1)
    c: Coincident(g2,g0)
    c: Coincident(g3,g2)
    c: PointOnObject(g3,g-1)
    c: Vertical(g3)
    c: Distance(g4) = 0.55
    c: Coincident(g4,g3)
    c: PointOnObject(g4,g-1)
    c: Distance(g5) = 2
    c: Coincident(g5,g4)
    c: Vertical(g5)
    c: Coincident(g6,g5)
    c: PointOnObject(g6,g-2)
    c: Horizontal(g6)
    c: Coincident(g7,g6)
    c: Coincident(g7,g0)
FEATURE [PartDesign::Revolution] Revolution004
  Angle = 360
  Angle2 = 60
  Axis = (0,1,0)
  Base = (0,0,0)
  Profile = -> Sketch018
  ReferenceAxis = -> Sketch018 [V_Axis]
  Refine = true
  Reversed = true
  Suppressed = false
  Type = 0
FEATURE [PartDesign::Body] Body008
  AllowCompound = false
  Group = -> [Sketch018,Revolution004]
  Origin = -> Origin017
  Tip = -> Revolution004
FEATURE [App::Part] Part001  label="Led10mm001"
  Group = -> [Body008]
  Origin = -> Origin016
  Placement = pos=(0,-3,40) rot=(0,0,1;0rad)
FEATURE [Sketcher::SketchObject] Sketch021
  ArcFitTolerance = 1e-06
  AttachmentSupport = -> [XY_Plane019]
  FullyConstrained = true
  MakeInternals = false
  MapMode = 5
  sketch-geometry (7):
    g0: LineSegment StartX=0 StartY=0 StartZ=0 EndX=0 EndY=-32 EndZ=0
    g1: LineSegment StartX=0 StartY=-32 StartZ=0 EndX=12 EndY=-32 EndZ=0
    g2: LineSegment StartX=12 StartY=-32 StartZ=0 EndX=12 EndY=0 EndZ=0
    g3: LineSegment StartX=0 StartY=0 StartZ=0 EndX=0 EndY=10 EndZ=0
    g4: LineSegment StartX=0 StartY=10 StartZ=0 EndX=27.75 EndY=10 EndZ=0
    g5: LineSegment StartX=12 StartY=0 StartZ=0 EndX=30 EndY=0 EndZ=0
    g6: LineSegment StartX=30 StartY=0 StartZ=0 EndX=27.75 EndY=10 EndZ=0
  constraints (20):
    c: Distance(g0) = 32
    c: Coincident(g0,g-1)
    c: PointOnObject(g0,g-2)
    c: Distance(g1) = 12
    c: Coincident(g1,g0)
    c: Horizontal(g1)
    c: Coincident(g2,g1)
    c: PointOnObject(g2,g-1)
    c: Vertical(g2)
    c: Distance(g3) = 10
    c: Coincident(g3,g0)
    c: PointOnObject(g3,g-2)
    c: Distance(g4) = 27.75
    c: Coincident(g4,g3)
    c: Horizontal(g4)
    c: Distance(g5) = 18
    c: Coincident(g5,g2)
    c: PointOnObject(g5,g-1)
    c: Coincident(g6,g5)
    c: Coincident(g6,g4)
FEATURE [Sketcher::SketchObject] Sketch023
  ArcFitTolerance = 1e-06
  FullyConstrained = false
  MakeInternals = false
  MapMode = 5
  Placement = pos=(0,0,0) rot=(1,0,0;1.5708rad)
  sketch-geometry (3):
    g0: LineSegment [constr] StartX=0 StartY=0 StartZ=0 EndX=18.75 EndY=0 EndZ=0
    g1: Circle CenterX=18.75 CenterY=0 CenterZ=0 NormalX=0 NormalY=0 NormalZ=1 AngleXU=0 Radius=1.75
    g2: Circle CenterX=-18.75 CenterY=0 CenterZ=0 NormalX=0 NormalY=0 NormalZ=1 AngleXU=0 Radius=1.75
  constraints (6):
    c: Distance(g0) = 18.75
    c: Coincident(g0,g-1)
    c: PointOnObject(g0,g-1)
    c: Diameter(g1) = 3.5
    c: Coincident(g1,g0)
    c: Diameter(g2) = 3.5
FEATURE [PartDesign::Revolution] Revolution005
  Angle = 360
  Angle2 = 60
  Axis = (0,1,0)
  Base = (0,0,0)
  Profile = -> Sketch021
  ReferenceAxis = -> Sketch021 [V_Axis]
  Refine = true
  Reversed = true
  Suppressed = false
  Type = 0
FEATURE [PartDesign::Pad] Pad012
  BaseFeature = -> Revolution005
  Direction = (0,-1,2e-16)
  Length = 3
  Length2 = 10
  Profile = -> Sketch023
  ReferenceAxis = -> Sketch023 [N_Axis]
  Refine = true
  Suppressed = false
  Type = 0
FEATURE [Sketcher::SketchObject] Sketch024
  ArcFitTolerance = 1e-06
  AttachmentSupport = -> [Pad012]
  FullyConstrained = true
  MakeInternals = false
  MapMode = 5
  Placement = pos=(0,-32,0) rot=(1,0,0;1.5708rad)
  sketch-geometry (4):
    g0: LineSegment StartX=-8.25 StartY=23.5 StartZ=0 EndX=-8.25 EndY=-14.5 EndZ=0
    g1: LineSegment StartX=-8.25 StartY=-14.5 StartZ=0 EndX=8.25 EndY=-14.5 EndZ=0
    g2: LineSegment StartX=8.25 StartY=-14.5 StartZ=0 EndX=8.25 EndY=23.5 EndZ=0
    g3: LineSegment StartX=8.25 StartY=23.5 StartZ=0 EndX=-8.25 EndY=23.5 EndZ=0
  constraints (12):
    c: Coincident(g0,g1)
    c: Coincident(g1,g2)
    c: Coincident(g2,g3)
    c: Coincident(g3,g0)
    c: Vertical(g0)
    c: Vertical(g2)
    c: Horizontal(g1)
    c: Horizontal(g3)
    c: Distance(g0,g2) = 16.5
    c: Distance(g1,g3) = 38
    c: Distance(g0,g-2) = 8.25
    c: Distance(g-1,g1) = 14.5
FEATURE [PartDesign::Pad] Pad013
  BaseFeature = -> Pad012
  Direction = (0,-1,2e-16)
  Length = 21.6
  Length2 = 10
  Profile = -> Sketch024
  ReferenceAxis = -> Sketch024 [N_Axis]
  Refine = true
  Suppressed = false
  Type = 0
FEATURE [PartDesign::Body] Body009
  AllowCompound = false
  Group = -> [Sketch021,Revolution005,Sketch023,Pad012,Sketch024,Pad013]
  Origin = -> Origin019
  Tip = -> Pad013
FEATURE [PartDesign::ShapeBinder] ReferenceRevolution005
  Support = -> [Revolution005]
  TraceSupport = false
FEATURE [Sketcher::SketchObject] Sketch025
  ArcFitTolerance = 1e-06
  AttachmentSupport = -> [ReferenceRevolution005]
  FullyConstrained = true
  MakeInternals = false
  MapMode = 5
  Placement = pos=(0,10,0) rot=(0,0.707107,0.707107;3.14159rad)
  sketch-geometry (1):
    g0: Circle CenterX=0 CenterY=0 CenterZ=0 NormalX=0 NormalY=0 NormalZ=1 AngleXU=0 Radius=25.75
  constraints (2):
    c: Diameter(g0) = 51.5
    c: Coincident(g0,g-1)
FEATURE [PartDesign::Pad] Pad014
  Direction = (0,1,-2e-16)
  Length = 4
  Length2 = 10
  Profile = -> Sketch025
  ReferenceAxis = -> Sketch025 [N_Axis]
  Refine = true
  Suppressed = false
  Type = 0
FEATURE [PartDesign::Body] Body010
  AllowCompound = false
  Group = -> [ReferenceRevolution005,Sketch025,Pad014]
  Origin = -> Origin020
  Tip = -> Pad014
FEATURE [App::Part] Part002  label="Button GMSI-1B-C"
  Group = -> [Body009,Body010]
  Origin = -> Origin018
  Placement = pos=(0,0,80) rot=(0,0,1;0rad)
FEATURE [Sketcher::SketchObject] Sketch026
  ArcFitTolerance = 1e-06
  AttachmentSupport = -> [XY_Plane022]
  FullyConstrained = true
  MakeInternals = false
  MapMode = 5
  sketch-geometry (7):
    g0: LineSegment StartX=0 StartY=0 StartZ=0 EndX=0 EndY=10.8 EndZ=0
    g1: LineSegment StartX=0 StartY=10.8 StartZ=0 EndX=13.8 EndY=10.8 EndZ=0
    g2: LineSegment StartX=13.8 StartY=10.8 StartZ=0 EndX=13.8 EndY=0 EndZ=0
    g3: LineSegment StartX=0 StartY=0 StartZ=0 EndX=0 EndY=-9 EndZ=0
    g4: LineSegment StartX=0 StartY=-9 StartZ=0 EndX=10.75 EndY=-9 EndZ=0
    g5: LineSegment StartX=10.75 StartY=-9 StartZ=0 EndX=10.75 EndY=0 EndZ=0
    g6: LineSegment StartX=10.75 StartY=0 StartZ=0 EndX=13.8 EndY=0 EndZ=0
  constraints (20):
    c: Distance(g0) = 10.8
    c: Coincident(g0,g-1)
    c: PointOnObject(g0,g-2)
    c: Distance(g1) = 13.8
    c: Coincident(g1,g0)
    c: Horizontal(g1)
    c: Coincident(g2,g1)
    c: PointOnObject(g2,g-1)
    c: Vertical(g2)
    c: Distance(g3) = 9
    c: Coincident(g3,g0)
    c: PointOnObject(g3,g-2)
    c: Distance(g4) = 10.75
    c: Coincident(g4,g3)
    c: Horizontal(g4)
    c: Coincident(g5,g4)
    c: PointOnObject(g5,g-1)
    c: Vertical(g5)
    c: Coincident(g6,g5)
    c: Coincident(g6,g2)
FEATURE [PartDesign::Revolution] Revolution006
  Angle = 360
  Angle2 = 60
  Axis = (0,1,0)
  Base = (0,0,0)
  Profile = -> Sketch026
  ReferenceAxis = -> Sketch026 [V_Axis]
  Refine = true
  Reversed = true
  Suppressed = false
  Type = 0
FEATURE [Sketcher::SketchObject] Sketch027
  ArcFitTolerance = 1e-06
  AttachmentSupport = -> [Revolution006]
  FullyConstrained = true
  MakeInternals = false
  MapMode = 5
  Placement = pos=(0,-9,0) rot=(1,0,0;1.5708rad)
  sketch-geometry (4):
    g0: LineSegment StartX=-15 StartY=20 StartZ=0 EndX=-15 EndY=-20 EndZ=0
    g1: LineSegment StartX=-15 StartY=-20 StartZ=0 EndX=15 EndY=-20 EndZ=0
    g2: LineSegment StartX=15 StartY=-20 StartZ=0 EndX=15 EndY=20 EndZ=0
    g3: LineSegment StartX=15 StartY=20 StartZ=0 EndX=-15 EndY=20 EndZ=0
  constraints (12):
    c: Coincident(g0,g1)
    c: Coincident(g1,g2)
    c: Coincident(g2,g3)
    c: Coincident(g3,g0)
    c: Vertical(g0)
    c: Vertical(g2)
    c: Horizontal(g1)
    c: Horizontal(g3)
    c: Distance(g0,g2) = 30
    c: Distance(g1,g3) = 40
    c: Distance(g-2,g0) = 15
    c: Distance(g1,g-1) = 20
FEATURE [PartDesign::Pad] Pad015
  BaseFeature = -> Revolution006
  Direction = (0,-1,2e-16)
  Length = 34
  Length2 = 10
  Profile = -> Sketch027
  ReferenceAxis = -> Sketch027 [N_Axis]
  Refine = true
  Suppressed = false
  Type = 0
FEATURE [PartDesign::Body] Body011  label="MainSteel"
  AllowCompound = false
  Group = -> [Sketch026,Revolution006,Sketch027,Pad015]
  Origin = -> Origin022
  Tip = -> Pad015
FEATURE [PartDesign::SubShapeBinder] Binder
  BindCopyOnChange = 0
  BindMode = 0
  ClaimChildren = false
  Context = -> Part003 [Body012.Binder.]
  Fuse = false
  MakeFace = true
  OffsetFill = false
  OffsetIntersection = false
  OffsetJoinType = 0
  OffsetOpenResult = false
  PartialLoad = false
  Refine = true
  Relative = true
  Support = -> [Body011[Pad015.Face1]]
  _Version = 2
FEATURE [Sketcher::SketchObject] Sketch028
  ArcFitTolerance = 1e-06
  AttachmentSupport = -> [XZ_Plane023]
  FullyConstrained = false
  MakeInternals = false
  MapMode = 5
  Placement = pos=(0,0,0) rot=(1,0,0;1.5708rad)
  sketch-geometry (9):
    g0: ArcOfCircle CenterX=0 CenterY=0 CenterZ=0 NormalX=0 NormalY=0 NormalZ=1 AngleXU=0 Radius=10.5 StartAngle=4.71239 EndAngle=4.71239
    g1: LineSegment [constr] StartX=0 StartY=0 StartZ=0 EndX=0 EndY=-10.5 EndZ=0
    g2: LineSegment [constr] StartX=0 StartY=-10.5 StartZ=0 EndX=0 EndY=-13 EndZ=0
    g3: ArcOfCircle CenterX=0 CenterY=-13 CenterZ=0 NormalX=0 NormalY=0 NormalZ=1 AngleXU=0 Radius=2.5 StartAngle=1.5708 EndAngle=1.5708
    g4: LineSegment [constr] StartX=0 StartY=-13 StartZ=0 EndX=2.5 EndY=-13 EndZ=0
    g5: LineSegment StartX=2.5 StartY=-13 StartZ=0 EndX=2.5 EndY=-10.198 EndZ=0
    g6: LineSegment StartX=-2.5 StartY=-13 StartZ=0 EndX=-2.5 EndY=-10.198 EndZ=0
    g7: ArcOfCircle CenterX=0 CenterY=-13 CenterZ=0 NormalX=0 NormalY=0 NormalZ=1 AngleXU=0 Radius=2.5 StartAngle=3.14159 EndAngle=6.28319
    g8: ArcOfCircle CenterX=0 CenterY=0 CenterZ=0 NormalX=0 NormalY=0 NormalZ=1 AngleXU=0 Radius=10.5 StartAngle=4.95279 EndAngle=10.7552
  constraints (25):
    c: Diameter(g0) = 21
    c: Coincident(g0,g-1)
    c: Coincident(g1,g0)
    c: PointOnObject(g1,g0)
    c: Vertical(g1)
    c: Distance(g2) = 2.5
    c: Coincident(g2,g1)
    c: PointOnObject(g2,g-2)
    c: Coincident(g3,g2)
    c: PointOnObject(g1,g3)
    c: Coincident(g4,g2)
    c: Horizontal(g4)
    c: Coincident(g5,g4)
    c: Vertical(g5)
    c: PointOnObject(g5,g8)
    c: Coincident(g7,g4)
    c: Equal(g3,g7)
    c: PointOnObject(g7,g6)
    c: Coincident(g3,g7)
    c: Coincident(g8,g6)
    c: Coincident(g0,g3)
    c: Equal(g0,g8)
    c: PointOnObject(g0,g3)
    c: PointOnObject(g8,g5)
    c: Coincident(g0,g8)
FEATURE [PartDesign::Pad] Pad016
  Direction = (0,-1,2e-16)
  Length = 7
  Length2 = 10
  Placement = pos=(0,0,0) rot=(1,0,0;1.5708rad)
  Profile = -> Sketch028
  ReferenceAxis = -> Sketch028 [N_Axis]
  Refine = true
  Reversed = true
  Suppressed = false
  Type = 0
FEATURE [PartDesign::Body] Body012  label="Plastic\"
  AllowCompound = false
  Group = -> [Binder,Sketch028,Pad016]
  Origin = -> Origin023
  Placement = pos=(0,10,0) rot=(0,0,1;0rad)
  Tip = -> Pad016
FEATURE [App::Part] Part003  label="Key"
  Group = -> [Body011,Body012]
  Origin = -> Origin021
  Placement = pos=(-2.04e-14,0,0) rot=(0,1,0;1.5708rad)
FEATURE [PartDesign::SubShapeBinder] Binder001
  BindCopyOnChange = 0
  BindMode = 0
  ClaimChildren = false
  Context = -> Part004 [Body013.Binder001.]
  Fuse = false
  MakeFace = true
  OffsetFill = false
  OffsetIntersection = false
  OffsetJoinType = 0
  OffsetOpenResult = false
  PartialLoad = false
  Refine = true
  Relative = true
  Support = -> [Part001[Body008.]]
  _Version = 2
FEATURE [PartDesign::SubShapeBinder] Binder002
  BindCopyOnChange = 0
  BindMode = 0
  ClaimChildren = false
  Context = -> Part004 [Body013.Binder002.]
  Fuse = false
  MakeFace = true
  OffsetFill = false
  OffsetIntersection = false
  OffsetJoinType = 0
  OffsetOpenResult = false
  PartialLoad = false
  Refine = true
  Relative = true
  Support = -> [Part]
  _Version = 2
FEATURE [PartDesign::SubShapeBinder] Binder003
  BindCopyOnChange = 0
  BindMode = 0
  ClaimChildren = false
  Context = -> Part004 [Body013.Binder003.]
  Fuse = false
  MakeFace = true
  OffsetFill = false
  OffsetIntersection = false
  OffsetJoinType = 0
  OffsetOpenResult = false
  PartialLoad = false
  Refine = true
  Relative = true
  Support = -> [Part003[Body011.Pad015.Face4]]
  _Version = 2
FEATURE [PartDesign::SubShapeBinder] Binder004
  BindCopyOnChange = 0
  BindMode = 0
  ClaimChildren = false
  Context = -> Part004 [Body013.Binder004.]
  Fuse = false
  MakeFace = true
  OffsetFill = false
  OffsetIntersection = false
  OffsetJoinType = 0
  OffsetOpenResult = false
  PartialLoad = false
  Refine = true
  Relative = true
  Support = -> [Part002[Body009.Pad013.Face2]]
  _Version = 2
FEATURE [PartDesign::SubShapeBinder] Binder005
  BindCopyOnChange = 0
  BindMode = 0
  ClaimChildren = false
  Context = -> Part004 [Body013.Binder005.]
  Fuse = false
  MakeFace = true
  OffsetFill = false
  OffsetIntersection = false
  OffsetJoinType = 0
  OffsetOpenResult = false
  PartialLoad = false
  Refine = true
  Relative = true
  Support = -> [Part002[Body009.Pad013.Face16,Body009.Pad013.Face17]]
  _Version = 2
FEATURE [Sketcher::SketchObject] Sketch029
  ArcFitTolerance = 1e-06
  AttachmentSupport = -> [XZ_Plane025]
  ExternalGeometry = -> [Binder002,Binder001,Binder003,Binder004,Binder005]
  FullyConstrained = false
  MakeInternals = false
  MapMode = 5
  Placement = pos=(0,0,0) rot=(1,0,0;1.5708rad)
  sketch-geometry (10):
    g0: LineSegment StartX=35 StartY=-20 StartZ=0 EndX=35 EndY=110 EndZ=0
    g1: LineSegment StartX=35 StartY=110 StartZ=0 EndX=-35 EndY=110 EndZ=0
    g2: LineSegment StartX=-35 StartY=110 StartZ=0 EndX=-35 EndY=-20 EndZ=0
    g3: LineSegment StartX=-35 StartY=-20 StartZ=0 EndX=35 EndY=-20 EndZ=0
    g4: Circle CenterX=0 CenterY=40 CenterZ=0 NormalX=0 NormalY=0 NormalZ=1 AngleXU=0 Radius=4.95
    g5: Circle CenterX=0 CenterY=25 CenterZ=0 NormalX=0 NormalY=0 NormalZ=1 AngleXU=0 Radius=4.95
    g6: Circle CenterX=0 CenterY=0 CenterZ=0 NormalX=0 NormalY=0 NormalZ=1 AngleXU=0 Radius=10.75
    g7: Circle CenterX=0 CenterY=80 CenterZ=0 NormalX=0 NormalY=0 NormalZ=1 AngleXU=0 Radius=12
    g8: Circle CenterX=-18.75 CenterY=80 CenterZ=0 NormalX=0 NormalY=0 NormalZ=1 AngleXU=0 Radius=2
    g9: Circle CenterX=18.75 CenterY=80 CenterZ=0 NormalX=0 NormalY=0 NormalZ=1 AngleXU=0 Radius=2
  constraints (21):
    c: Coincident(g0,g1)
    c: Coincident(g1,g2)
    c: Coincident(g2,g3)
    c: Coincident(g3,g0)
    c: Vertical(g0)
    c: Vertical(g2)
    c: Horizontal(g1)
    c: Horizontal(g3)
    c: DistanceX(g3,g3) = 70
    c: Distance(g0,g-2) = 35
    c: DistanceY(g2,g2) = 130
    c: Distance(g3,g-1) = 20
    c: Coincident(g4,g-7)
    c: Coincident(g5,g-6)
    c: Equal(g5,g-3)
    c: Equal(g4,g-4)
    c: Tangent(g-9,g7) = -1.5708
    c: Coincident(g8,g-11)
    c: Coincident(g9,g-10)
    c: Diameter(g9) = 4
    c: Diameter(g8) = 4
FEATURE [PartDesign::Pad] Pad017
  Direction = (0,-1,2e-16)
  Length = 3
  Length2 = 10
  Placement = pos=(0,0,0) rot=(1,0,0;1.5708rad)
  Profile = -> Sketch029
  ReferenceAxis = -> Sketch029 [N_Axis]
  Refine = true
  Suppressed = false
  Type = 0
FEATURE [Sketcher::SketchObject] Sketch030
  ArcFitTolerance = 1e-06
  AttachmentSupport = -> [Pad017]
  ExternalGeometry = -> [Pad017]
  FullyConstrained = true
  MakeInternals = false
  MapMode = 5
  Placement = pos=(0,-3,0) rot=(1,0,0;1.5708rad)
  sketch-geometry (8):
    g0: LineSegment StartX=-35 StartY=-20 StartZ=0 EndX=35 EndY=-20 EndZ=0
    g1: LineSegment StartX=35 StartY=-20 StartZ=0 EndX=35 EndY=110 EndZ=0
    g2: LineSegment StartX=35 StartY=110 StartZ=0 EndX=-35 EndY=110 EndZ=0
    g3: LineSegment StartX=-35 StartY=110 StartZ=0 EndX=-35 EndY=-20 EndZ=0
    g4: LineSegment StartX=-32 StartY=-17 StartZ=0 EndX=32 EndY=-17 EndZ=0
    g5: LineSegment StartX=32 StartY=-17 StartZ=0 EndX=32 EndY=107 EndZ=0
    g6: LineSegment StartX=32 StartY=107 StartZ=0 EndX=-32 EndY=107 EndZ=0
    g7: LineSegment StartX=-32 StartY=107 StartZ=0 EndX=-32 EndY=-17 EndZ=0
  constraints (22):
    c: Coincident(g0,g1)
    c: Coincident(g1,g2)
    c: Coincident(g2,g3)
    c: Coincident(g3,g0)
    c: Horizontal(g0)
    c: Horizontal(g2)
    c: Vertical(g1)
    c: Vertical(g3)
    c: Coincident(g0,g-4)
    c: Coincident(g1,g-6)
    c: Coincident(g4,g5)
    c: Coincident(g5,g6)
    c: Coincident(g6,g7)
    c: Coincident(g7,g4)
    c: Horizontal(g4)
    c: Horizontal(g6)
    c: Vertical(g5)
    c: Vertical(g7)
    c: Distance(g1,g5) = 3
    c: Distance(g2,g6) = 3
    c: Distance(g0,g4) = 3
    c: Distance(g3,g7) = 3
FEATURE [PartDesign::Pad] Pad018
  BaseFeature = -> Pad017
  Direction = (0,-1,2e-16)
  Length = 60
  Length2 = 10
  Placement = pos=(0,0,0) rot=(1,0,0;1.5708rad)
  Profile = -> Sketch030
  ReferenceAxis = -> Sketch030 [N_Axis]
  Refine = true
  Suppressed = false
  Type = 0
FEATURE [PartDesign::SubShapeBinder] Binder006
  BindCopyOnChange = 0
  BindMode = 0
  ClaimChildren = false
  Context = -> Part004 [Body013.Binder006.]
  Fuse = false
  MakeFace = true
  OffsetFill = false
  OffsetIntersection = false
  OffsetJoinType = 0
  OffsetOpenResult = false
  PartialLoad = false
  Refine = true
  Relative = true
  Support = -> [Assembly[Body005.Pocket001.Face10,Body005.Pocket001.Face9,Body005.Pocket001.Face11,Body005.Pocket001.Face12]]
  _Version = 2
FEATURE [Sketcher::SketchObject] Sketch031
  ArcFitTolerance = 1e-06
  AttachmentSupport = -> [Pad018]
  ExternalGeometry = -> [Binder006]
  FullyConstrained = true
  MakeInternals = false
  MapMode = 5
  Placement = pos=(35,0,0) rot=(0.707107,0,0.707107;3.14159rad)
  sketch-geometry (4):
    g0: ArcOfCircle CenterX=45 CenterY=45 CenterZ=0 NormalX=0 NormalY=0 NormalZ=1 AngleXU=0 Radius=5.4 StartAngle=2.12208 EndAngle=4.1611
    g1: ArcOfCircle CenterX=45 CenterY=45 CenterZ=0 NormalX=0 NormalY=0 NormalZ=1 AngleXU=0 Radius=5.4 StartAngle=5.26367 EndAngle=7.3027
    g2: LineSegment StartX=42.1716 StartY=49.6 StartZ=0 EndX=47.8284 EndY=49.6 EndZ=0
    g3: LineSegment StartX=42.1716 StartY=40.4 StartZ=0 EndX=47.8284 EndY=40.4 EndZ=0
  constraints (10):
    c: Coincident(g0,g-8)
    c: Coincident(g0,g-4)
    c: Coincident(g1,g0)
    c: Coincident(g1,g-7)
    c: Coincident(g2,g0)
    c: Coincident(g2,g1)
    c: Horizontal(g2)
    c: Coincident(g3,g0)
    c: Coincident(g3,g1)
    c: Horizontal(g3)
FEATURE [PartDesign::Pocket] Pocket
  BaseFeature = -> Pad018
  Direction = (-1,0,2e-16)
  Length = 5
  Length2 = 5
  Placement = pos=(0,0,0) rot=(1,0,0;1.5708rad)
  Profile = -> Sketch031
  ReferenceAxis = -> Sketch031 [N_Axis]
  Refine = true
  Suppressed = false
  Type = 2
FEATURE [PartDesign::Fillet] Fillet
  Base = -> Pocket [Edge3,Edge4,Edge1,Edge2]
  BaseFeature = -> Pocket
  Placement = pos=(0,0,0) rot=(1,0,0;1.5708rad)
  Radius = 2
  Refine = true
  SupportTransform = false
  Suppressed = false
  UseAllEdges = false
FEATURE [PartDesign::Body] Body013  label="Top"
  AllowCompound = false
  Group = -> [Sketch029,Binder001,Binder002,Binder003,Binder004,Pad017,Binder005,Sketch030,Pad018,Binder006,Sketch031,Pocket,Fillet]
  Origin = -> Origin025
  Tip = -> Fillet
FEATURE [PartDesign::SubShapeBinder] Binder007
  BindCopyOnChange = 0
  BindMode = 0
  ClaimChildren = false
  Context = -> Part004 [Body014.Binder007.]
  Fuse = false
  MakeFace = true
  OffsetFill = false
  OffsetIntersection = false
  OffsetJoinType = 0
  OffsetOpenResult = false
  PartialLoad = false
  Refine = true
  Relative = true
  Support = -> [Body013[Pad018.Face10]]
  _Version = 2
FEATURE [Sketcher::SketchObject] Sketch032
  ArcFitTolerance = 1e-06
  AttachmentSupport = -> [XZ_Plane026]
  ExternalGeometry = -> [Binder007]
  FullyConstrained = true
  MakeInternals = false
  MapMode = 5
  Placement = pos=(0,0,0) rot=(1,0,0;1.5708rad)
  sketch-geometry (4):
    g0: LineSegment StartX=-32 StartY=107 StartZ=0 EndX=-32 EndY=-17 EndZ=0
    g1: LineSegment StartX=-32 StartY=-17 StartZ=0 EndX=32 EndY=-17 EndZ=0
    g2: LineSegment StartX=32 StartY=-17 StartZ=0 EndX=32 EndY=107 EndZ=0
    g3: LineSegment StartX=32 StartY=107 StartZ=0 EndX=-32 EndY=107 EndZ=0
  constraints (10):
    c: Coincident(g0,g1)
    c: Coincident(g1,g2)
    c: Coincident(g2,g3)
    c: Coincident(g3,g0)
    c: Vertical(g0)
    c: Vertical(g2)
    c: Horizontal(g1)
    c: Horizontal(g3)
    c: Coincident(g0,g-5)
    c: Coincident(g1,g-10)
FEATURE [PartDesign::Pad] Pad019
  Direction = (0,-1,2e-16)
  Length = 5
  Length2 = 10
  Placement = pos=(0,0,0) rot=(1,0,0;1.5708rad)
  Profile = -> Sketch032
  ReferenceAxis = -> Sketch032 [N_Axis]
  Refine = true
  Reversed = true
  Suppressed = false
  Type = 0
FEATURE [Sketcher::SketchObject] Sketch033
  ArcFitTolerance = 1e-06
  AttachmentSupport = -> [XZ_Plane026]
  ExternalGeometry = -> [Pad019,Binder007]
  FullyConstrained = true
  MakeInternals = false
  MapMode = 5
  Placement = pos=(0,0,0) rot=(1,0,0;1.5708rad)
  sketch-geometry (4):
    g0: LineSegment StartX=-37.5 StartY=112.5 StartZ=0 EndX=-37.5 EndY=-22.5 EndZ=0
    g1: LineSegment StartX=-37.5 StartY=-22.5 StartZ=0 EndX=37.5 EndY=-22.5 EndZ=0
    g2: LineSegment StartX=37.5 StartY=-22.5 StartZ=0 EndX=37.5 EndY=112.5 EndZ=0
    g3: LineSegment StartX=37.5 StartY=112.5 StartZ=0 EndX=-37.5 EndY=112.5 EndZ=0
  constraints (12):
    c: Coincident(g0,g1)
    c: Coincident(g1,g2)
    c: Coincident(g2,g3)
    c: Coincident(g3,g0)
    c: Vertical(g0)
    c: Vertical(g2)
    c: Horizontal(g1)
    c: Horizontal(g3)
    c: Distance(g-2,g2) = 37.5
    c: Distance(g-2,g0) = 37.5
    c: Distance(g-4,g1) = 5.5
    c: Distance(g-3,g3) = 5.5
FEATURE [PartDesign::Pad] Pad020
  BaseFeature = -> Pad019
  Direction = (0,-1,2e-16)
  Length = 5
  Length2 = 10
  Placement = pos=(0,0,0) rot=(1,0,0;1.5708rad)
  Profile = -> Sketch033
  ReferenceAxis = -> Sketch033 [N_Axis]
  Refine = true
  Suppressed = false
  Type = 0
FEATURE [PartDesign::Fillet] Fillet001
  Base = -> Pad020 [Edge13,Edge11,Edge14,Edge16,Edge10,Edge12,Edge7,Edge4]
  BaseFeature = -> Pad020
  Placement = pos=(0,0,0) rot=(1,0,0;1.5708rad)
  Radius = 1
  Refine = true
  SupportTransform = false
  Suppressed = false
  UseAllEdges = false
FEATURE [Sketcher::SketchObject] Sketch034
  ArcFitTolerance = 1e-06
  AttachmentSupport = -> [Fillet001]
  ExternalGeometry = -> [Fillet001]
  FullyConstrained = false
  MakeInternals = false
  MapMode = 5
  Placement = pos=(0,-5,0) rot=(1,0,0;1.5708rad)
  sketch-geometry (4):
    g0: Circle CenterX=-27.5 CenterY=102.5 CenterZ=0 NormalX=0 NormalY=0 NormalZ=1 AngleXU=0 Radius=8.1
    g1: Circle CenterX=27.5 CenterY=102.5 CenterZ=0 NormalX=0 NormalY=0 NormalZ=1 AngleXU=0 Radius=8.1
    g2: Circle CenterX=-27.5 CenterY=-12.5 CenterZ=0 NormalX=0 NormalY=0 NormalZ=1 AngleXU=0 Radius=8.1
    g3: Circle CenterX=27.5 CenterY=-12.5 CenterZ=0 NormalX=0 NormalY=0 NormalZ=1 AngleXU=0 Radius=8.1
  constraints (8):
    c: Diameter(g0) = 16.2
    c: Distance(g0,g-4) = 10
    c: Distance(g0,g-6) = 10
    c: Diameter(g1) = 16.2
    c: Diameter(g2) = 16.2
    c: Distance(g2,g-4) = 10
    c: Distance(g2,g-3) = 10
    c: Diameter(g3) = 16.2
FEATURE [PartDesign::Pocket] Pocket002
  BaseFeature = -> Fillet001
  Direction = (0,1,-2e-16)
  Length = 1
  Length2 = 5
  Placement = pos=(0,0,0) rot=(1,0,0;1.5708rad)
  Profile = -> Sketch034
  ReferenceAxis = -> Sketch034 [N_Axis]
  Refine = true
  Suppressed = false
  Type = 0
FEATURE [PartDesign::Body] Body014  label="Bottom"
  AllowCompound = false
  Group = -> [Binder007,Sketch032,Pad019,Sketch033,Pad020,Fillet001,Sketch034,Pocket002]
  Origin = -> Origin026
  Placement = pos=(0,-63,0) rot=(0,0,1;0rad)
  Tip = -> Pocket002
FEATURE [App::Part] Part004  label="Case"
  Group = -> [Body013,Body014]
  Origin = -> Origin024
